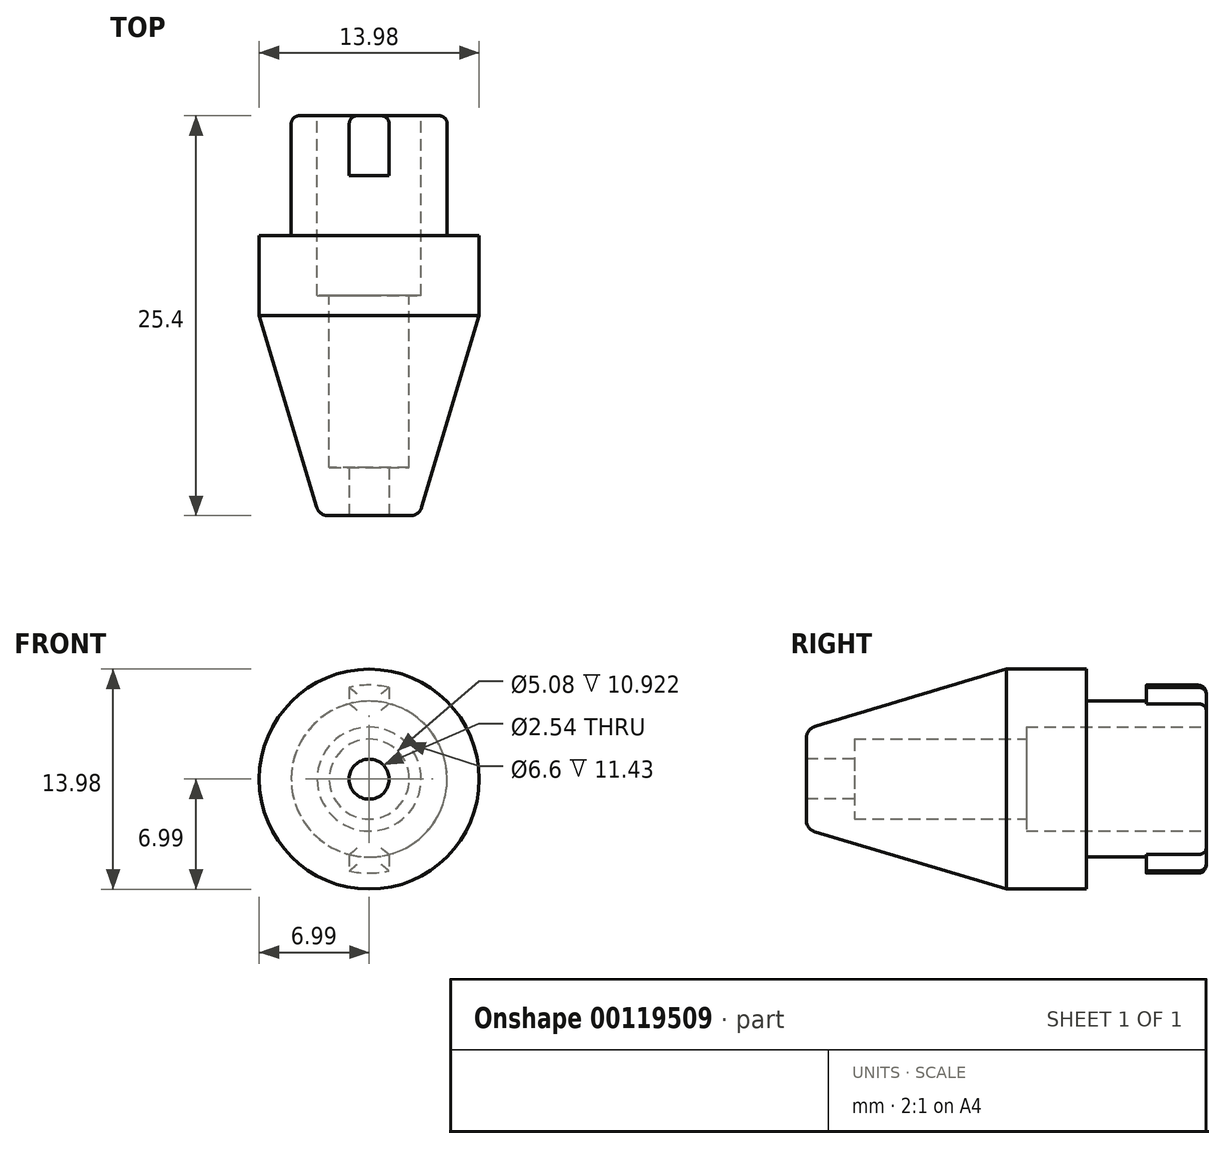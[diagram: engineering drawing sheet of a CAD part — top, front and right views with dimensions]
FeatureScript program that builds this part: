
annotation { "Feature Type Name" : "Feature", "Feature Type Description" : "" }
export const myFeature = defineFeature(function(context is Context, id is Id, definition is map)
    precondition{}
    {
        {
            var Q0;
            Q0=qCreatedBy(makeId("Right.planeOp"),FACE);
            var sketch = newSketch(context, id + "F0", { "sketchPlane" : qUnion([Q0])});
            skLineSegment(sketch, "E0", {"start": v(-43.5, 3.18) * mm, "end": v(-30.8, 6.99) * mm});
            skLineSegment(sketch, "E1", {"start": v(-30.8, 6.99) * mm, "end": v(-25.71, 6.99) * mm});
            skLineSegment(sketch, "E2", {"start": v(-43.5, 3.17) * mm, "end": v(-43.5, 0) * mm});
            skLineSegment(sketch, "E3", {"start": v(-43.5, 0) * mm, "end": v(-18.1, 0) * mm});
            skLineSegment(sketch, "E4", {"start": v(-18.1, 0) * mm, "end": v(-18.1, 4.95) * mm});
            skLineSegment(sketch, "E5", {"start": v(-25.71, 6.99) * mm, "end": v(-25.71, 4.95) * mm});
            skLineSegment(sketch, "E6", {"start": v(-25.71, 4.95) * mm, "end": v(-18.1, 4.95) * mm});
            skPoint(sketch, "E7.orphan", {"position": v(-18.1, 6.99) * mm});
            skSolve(sketch);
        }
        {
            var Q0;
            Q0=makeQuery(id+"F0.imprint","IMPRINT",FACE,{"disambiguationData":[TD([[makeQuery(id+"F0.imprint","IMPRINT",EDGE,{"derivedFrom":sQuery(id+"F0.wireOp",EDGE,"E0")}),-1.0]])]});
            var Q1;
            Q1=sQuery(id+"F0.wireOp",EDGE,"E3");
            revolve(context, id + "F1", {"entities" : qUnion([Q0]), "axis" : qUnion([Q1]), "revolveType" : RevolveType.FULL});
        }
        {
            var Q0;
            Q0=makeQuery(id+"F1.opRevolve","SWEPT_FACE",FACE,{"disambiguationData":[OSD([sQuery(id+"F0.wireOp",EDGE,"E2")])]});
            var sketch = newSketch(context, id + "F2", { "sketchPlane" : qUnion([Q0])});
            skCircle(sketch, "E8", {"center": v(0, 0) * mm, "radius": 1.27 * mm});
            skSolve(sketch);
        }
        {
            var Q0;
            Q0 = qSketchRegion(id + "F2", true);
            extrude(context, id + "F3", {"entities" : qUnion([Q0]), "operationType" : NewBodyOperationType.REMOVE, "endBound" : BoundingType.THROUGH_ALL, "oppositeDirection" : true, "depth" : 25.4 * mm});
        }
        {
            var Q0;
            Q0=makeQuery(id+"F1.opRevolve","SWEPT_EDGE",EDGE,{"disambiguationData":[OSD([sQuery(id+"F0.wireOp",EDGE,"E0"),sQuery(id+"F0.wireOp",EDGE,"E2")])]});
            fillet(context, id + "F4", {"entities" : qUnion([Q0]), "radius" : 0.76 * mm, "tangentPropagation" : true, "allowEdgeOverflow" : false});
        }
        {
            var Q0;
            Q0=makeQuery(id+"F1.opRevolve","SWEPT_FACE",FACE,{"disambiguationData":[OSD([sQuery(id+"F0.wireOp",EDGE,"E4")])]});
            var sketch = newSketch(context, id + "F5", { "sketchPlane" : qUnion([Q0])});
            skCircle(sketch, "E9", {"center": v(0, 0) * mm, "radius": 2.54 * mm});
            skSolve(sketch);
        }
        {
            var Q0;
            Q0 = qSketchRegion(id + "F5", true);
            extrude(context, id + "F6", {"entities" : qUnion([Q0]), "operationType" : NewBodyOperationType.REMOVE, "oppositeDirection" : true, "depth" : 22.35 * mm});
        }
        {
            var Q0;
            Q0=makeQuery(id+"F1.opRevolve","SWEPT_FACE",FACE,{"disambiguationData":[OSD([sQuery(id+"F0.wireOp",EDGE,"E4")])]});
            var sketch = newSketch(context, id + "F7", { "sketchPlane" : qUnion([Q0])});
            skArc(sketch, "E10", {"start": v(-1.27, -5.83) * mm, "mid": v(0, -5.97) * mm, "end": v(1.27, -5.83) * mm});
            skLineSegment(sketch, "E11.left", {"start": v(-1.27, 5.83) * mm, "end": v(-1.27, 4.58) * mm});
            skLineSegment(sketch, "E11.right", {"start": v(1.27, 5.83) * mm, "end": v(1.27, 4.58) * mm});
            skArc(sketch, "E12", {"start": v(-1.27, -4.58) * mm, "mid": v(0, -4.75) * mm, "end": v(1.27, -4.58) * mm});
            skLineSegment(sketch, "E13.trimOffspring", {"start": v(-1.27, -4.58) * mm, "end": v(-1.27, -5.83) * mm});
            skLineSegment(sketch, "E14.trimOffspring", {"start": v(1.27, -4.58) * mm, "end": v(1.27, -5.83) * mm});
            skArc(sketch, "E15.trimOffspring", {"start": v(1.27, 4.58) * mm, "mid": v(0, 4.75) * mm, "end": v(-1.27, 4.58) * mm});
            skArc(sketch, "E16.trimOffspring", {"start": v(1.27, 5.83) * mm, "mid": v(0, 5.97) * mm, "end": v(-1.27, 5.83) * mm});
            skSolve(sketch);
        }
        {
            var Q0;
            Q0 = qSketchRegion(id + "F7", true);
            extrude(context, id + "F8", {"entities" : qUnion([Q0]), "operationType" : NewBodyOperationType.ADD, "oppositeDirection" : true, "depth" : 3.8 * mm});
        }
        {
            var Q0;
            {var subQ1=sQuery(id+"F0.wireOp",EDGE,"E6");var subQ2=sQuery(id+"F7.wireOp",EDGE,"E11.left");var subQ3=sQuery(id+"F0.wireOp",EDGE,"E4");Q0=makeQuery(id+"F8.boolean.opBoolean","SPLIT",EDGE,{"disambiguationData":[TD([makeQuery(id+"F8.opExtrude","SWEPT_FACE",FACE,{"disambiguationData":[OSD([subQ2])]})])],"derivedFrom":makeQuery(id+"F1.opRevolve","SWEPT_EDGE",EDGE,{"disambiguationData":[OSD([subQ3,subQ1])]})});}
            var Q1;
            {var subQ0=sQuery(id+"F7.wireOp",EDGE,"E11.right");var subQ2=sQuery(id+"F0.wireOp",EDGE,"E6");var subQ3=sQuery(id+"F0.wireOp",EDGE,"E4");Q1=makeQuery(id+"F8.boolean.opBoolean","SPLIT",EDGE,{"disambiguationData":[TD([makeQuery(id+"F8.opExtrude","SWEPT_FACE",FACE,{"disambiguationData":[OSD([subQ0])]})])],"derivedFrom":makeQuery(id+"F1.opRevolve","SWEPT_EDGE",EDGE,{"disambiguationData":[OSD([subQ3,subQ2])]})});}
            var Q2;
            Q2=makeQuery(id+"F8.opExtrude","CAP_EDGE",EDGE,{"disambiguationData":[OSD([sQuery(id+"F7.wireOp",EDGE,"E11.left")])],"isStart":true});
            var Q3;
            Q3=makeQuery(id+"F8.opExtrude","CAP_EDGE",EDGE,{"disambiguationData":[OSD([sQuery(id+"F7.wireOp",EDGE,"E11.right")])],"isStart":true});
            var Q4;
            Q4=makeQuery(id+"F8.opExtrude","CAP_EDGE",EDGE,{"disambiguationData":[OSD([sQuery(id+"F7.wireOp",EDGE,"E16.trimOffspring")])],"isStart":true});
            var Q5;
            Q5=makeQuery(id+"F8.opExtrude","CAP_EDGE",EDGE,{"disambiguationData":[OSD([sQuery(id+"F7.wireOp",EDGE,"E10")])],"isStart":true});
            var Q6;
            Q6=makeQuery(id+"F8.opExtrude","CAP_EDGE",EDGE,{"disambiguationData":[OSD([sQuery(id+"F7.wireOp",EDGE,"E14.trimOffspring")])],"isStart":true});
            var Q7;
            Q7=makeQuery(id+"F8.opExtrude","CAP_EDGE",EDGE,{"disambiguationData":[OSD([sQuery(id+"F7.wireOp",EDGE,"E13.trimOffspring")])],"isStart":true});
            fillet(context, id + "F9", {"entities" : qUnion([Q0, Q1, Q2, Q3, Q4, Q5, Q6, Q7]), "radius" : 0.5 * mm, "tangentPropagation" : true, "allowEdgeOverflow" : false});
        }
        {
            var Q0;
            Q0=makeQuery(id+"F8.boolean.opBoolean","MERGE",FACE,{"derivedFrom":[makeQuery(id+"F1.opRevolve","SWEPT_FACE",FACE,{"disambiguationData":[OSD([sQuery(id+"F0.wireOp",EDGE,"E4")])]}),makeQuery(id+"F8.opExtrude","CAP_FACE",FACE,{"disambiguationData":[OSD([sQuery(id+"F7.wireOp",EDGE,"E10"),sQuery(id+"F7.wireOp",EDGE,"E12"),sQuery(id+"F7.wireOp",EDGE,"E13.trimOffspring"),sQuery(id+"F7.wireOp",EDGE,"E14.trimOffspring")])],"isStart":true}),makeQuery(id+"F8.opExtrude","CAP_FACE",FACE,{"disambiguationData":[OSD([sQuery(id+"F7.wireOp",EDGE,"E11.left"),sQuery(id+"F7.wireOp",EDGE,"E11.right"),sQuery(id+"F7.wireOp",EDGE,"E15.trimOffspring"),sQuery(id+"F7.wireOp",EDGE,"E16.trimOffspring")])],"isStart":true})]});
            var sketch = newSketch(context, id + "F10", { "sketchPlane" : qUnion([Q0])});
            skCircle(sketch, "E17", {"center": v(0, 0) * mm, "radius": 3.3 * mm});
            skSolve(sketch);
        }
        {
            var Q0;
            Q0 = qSketchRegion(id + "F10", true);
            extrude(context, id + "F11", {"entities" : qUnion([Q0]), "operationType" : NewBodyOperationType.REMOVE, "oppositeDirection" : true, "depth" : 11.43 * mm});
        }
    });
